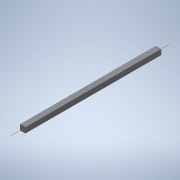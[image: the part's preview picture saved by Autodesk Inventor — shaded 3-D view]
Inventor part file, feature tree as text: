
AUTODESK INVENTOR PART (.ipt)
format: ipt  version: 2020 (Build 240168000, 168)  size: 181,248 bytes
history: native  units: in
note: dims shown in document units (in); Inventor stores cm internally (conversion verified against a paired STEP export)
features: other x6, extrude x1, imported_body x1, sketch x1
ambient origin geometry x8: Origin, YZ Plane, XZ Plane, XY Plane, X Axis, Y Axis, Z Axis, Center Point
bodies: Body1 (feature_tree)
feature tree (9):
  other  "Shaft 3.0 inch"
  parser-record x1  (decoder bookkeeping rows leaked as tree rows — omitted from the tree; the rows remain in map.json)
  other  "Shaft"
  extrude  "length cut"  Depth=3.0in
  other  "front plane"
  imported_body  "Base1"
  sketch  "Sketch1"  dims[d1=0.0in d2=3.0in d3=0.0in d4=0.0in d5=0.0in]
  other  "main axis"
  other  "back plane"
